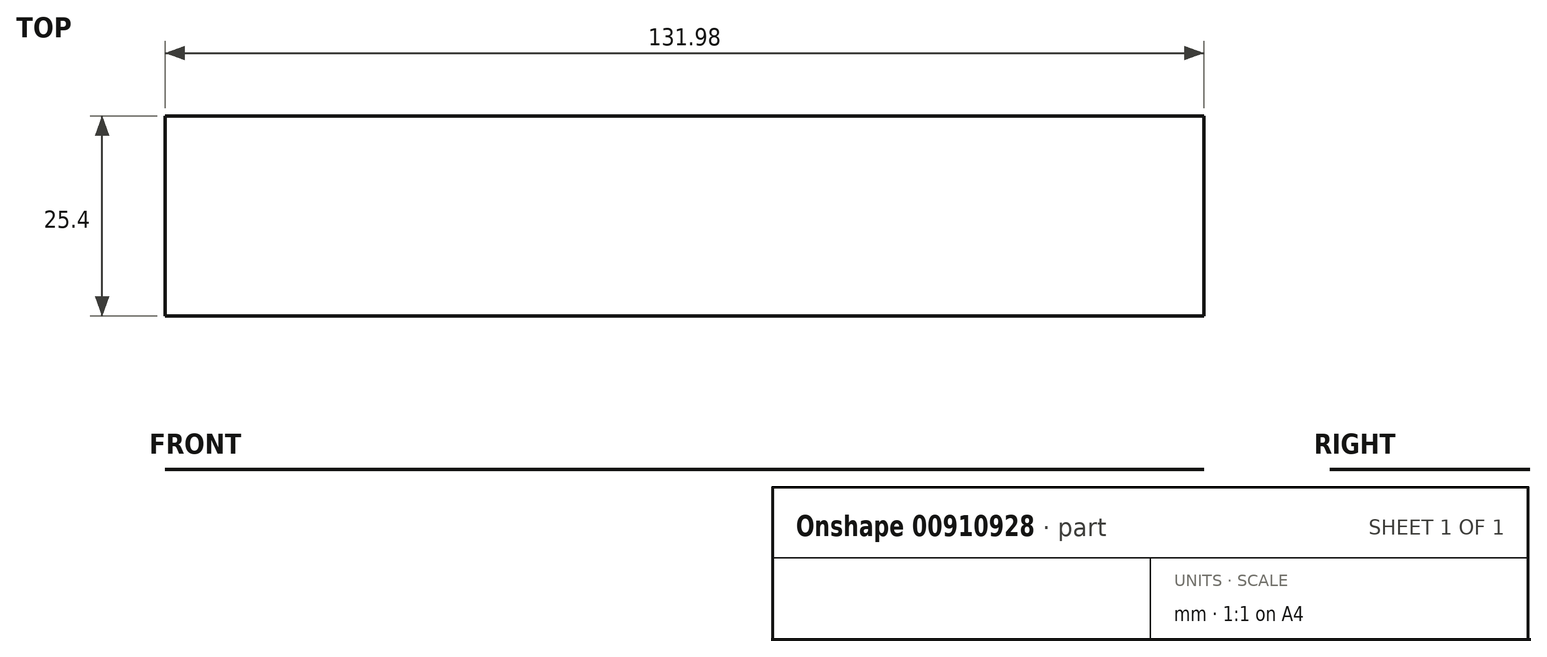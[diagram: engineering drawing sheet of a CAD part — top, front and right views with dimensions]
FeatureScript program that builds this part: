
annotation { "Feature Type Name" : "Feature", "Feature Type Description" : "" }
export const myFeature = defineFeature(function(context is Context, id is Id, definition is map)
    precondition{}
    {
        {
            var Q0;
            Q0=qCreatedBy(makeId("Front.planeOp"),FACE);
            var sketch = newSketch(context, id + "F0", { "sketchPlane" : qUnion([Q0])});
            skLineSegment(sketch, "E0.bottom", {"start": v(-66, 17.27) * mm, "end": v(66, 17.27) * mm});
            skLineSegment(sketch, "E0.top", {"start": v(-66, -17.27) * mm, "end": v(66, -17.27) * mm});
            skLineSegment(sketch, "E0.left", {"start": v(-66, 17.27) * mm, "end": v(-66, -17.27) * mm});
            skLineSegment(sketch, "E0.right", {"start": v(66, 17.27) * mm, "end": v(66, -17.27) * mm});
            skPoint(sketch, "E0.middle", {"position": v(0, 0) * mm});
            skLineSegment(sketch, "E1.bottom", {"start": v(90.12, 96.74) * mm, "end": v(150.67, 96.74) * mm});
            skLineSegment(sketch, "E1.top", {"start": v(90.12, 55.11) * mm, "end": v(150.67, 55.11) * mm});
            skLineSegment(sketch, "E1.left", {"start": v(90.12, 96.74) * mm, "end": v(90.12, 55.11) * mm});
            skLineSegment(sketch, "E1.right", {"start": v(150.67, 96.74) * mm, "end": v(150.67, 55.11) * mm});
            skPoint(sketch, "E1.middle", {"position": v(120.4, 75.92) * mm});
            skLineSegment(sketch, "E2", {"start": v(66, 17.27) * mm, "end": v(66, 50.38) * mm});
            skArc(sketch, "E3", {"start": v(66, 50.38) * mm, "mid": v(69.08, 60.81) * mm, "end": v(77.34, 67.88) * mm});
            skSolve(sketch);
        }
        {
            var Q0;
            Q0=sQuery(id+"F0.wireOp",EDGE,"E0.top");
            extrude(context, id + "F1", {"bodyType" : ToolBodyType.SURFACE, "surfaceEntities" : qUnion([Q0]), "depth" : 25.4 * mm, "offsetDistance" : 25.4 * mm});
        }
    });
